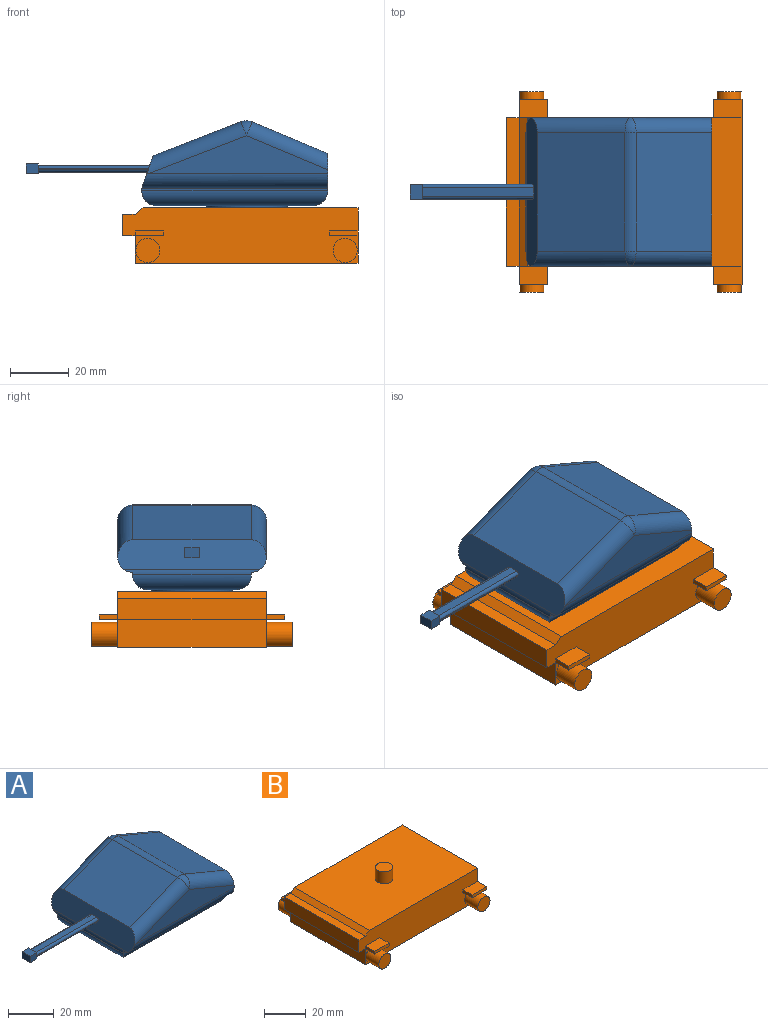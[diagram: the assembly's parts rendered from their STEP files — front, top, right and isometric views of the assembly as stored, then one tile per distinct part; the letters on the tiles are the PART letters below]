
ASSEMBLY  parts=2 mates=1
PART A: 41 faces, bbox 105.1x50.8x29.8 mm
  f0: cylinder r=11.12mm len=22.25mm, axis (0,0,1), area 471.8mm2, adj f2,f3
  f1: cylinder r=13.89mm len=27.79mm, axis (0,0,1), area 65.5mm2, adj f2,f7
  f2: plane 27.79x27.79mm, normal (0,0,-1), area 217.6mm2, adj f0,f1
  f3: plane 22.25x22.25mm, normal (0,0,-1), area 388.8mm2, adj f0
  f4: plane 40.64x0.05mm, normal (-1,0,0), area 2.2mm2, adj f5,f6,f36,f40
  f5: plane 63.5x0.92mm, normal (0,1,0), area 58.4mm2, adj f4,f33,f34,f38,f40
  f6: plane 63.5x0.92mm, normal (0,-1,0), area 58.4mm2, adj f4,f32,f33,f37,f40
  f7: plane 53.34x30.48mm, normal (0,0,-1), area 1019.4mm2, adj f1,f36,f37,f38,f39
  f8: plane 5.08x1.62mm, normal (1,0,0), area 3.5mm2, adj f9,f19,f20,f21,f22,f23
  f9: plane 5.08x4.19mm, normal (0,0,-1), area 21.3mm2, adj f8,f10,f19,f23
  f10: plane 5.08x3.37mm, normal (-1,0,0), area 17.1mm2, adj f9,f11,f19,f23
  f11: plane 5.08x4.19mm, normal (0,0,1), area 21.3mm2, adj f10,f12,f19,f23
  f12: plane 5.08x1.62mm, normal (1,0,0), area 3.5mm2, adj f11,f16,f17,f18,f19,f23
  f13: cylinder r=5.08mm len=40.64mm, axis (0,1,0), area 158.4mm2, adj f14,f15,f24,f27
  f14: sphere r=5.08mm, area 19.8mm2, adj f13,f25,f28
  f15: sphere r=5.08mm, area 19.8mm2, adj f13,f26,f30
  f16: cylinder r=1.02mm len=38.1mm, axis (1,0,0), area 60.6mm2, adj f12,f17,f23,f35
  f17: plane 38.1x3.05mm, normal (0,0,1), area 116.1mm2, adj f12,f16,f18,f35
  f18: cylinder r=1.02mm len=38.1mm, axis (-1,0,0), area 60.6mm2, adj f12,f17,f19,f35
  f19: plane 41.93x3.37mm, normal (0,1,0), area 19.4mm2, adj f8,f9,f10,f11,f12,f18,f20,f35
  f20: cylinder r=1.02mm len=37.69mm, axis (1,0,0), area 59.8mm2, adj f8,f19,f21,f35
  f21: plane 37.34x3.05mm, normal (0,0,-1), area 113.8mm2, adj f8,f20,f22,f35
  f22: cylinder r=1.02mm len=37.69mm, axis (-1,0,0), area 59.8mm2, adj f8,f21,f23,f35
  f23: plane 41.93x3.37mm, normal (0,-1,0), area 19.4mm2, adj f8,f9,f10,f11,f12,f16,f22,f35
  f24: plane 40.64x30.03mm, normal (-0.36,0,0.93), area 1309.1mm2, adj f13,f25,f30,f35
  f25: cylinder r=5.08mm len=35.79mm, axis (-0.93,0,-0.36), area 269.6mm2, adj f14,f24,f29,f34,f35
  f26: cylinder r=5.08mm len=29.72mm, axis (0.92,0,-0.39), area 229.4mm2, adj f15,f27,f31,f33
  f27: plane 40.64x25.79mm, normal (0.39,0,0.92), area 1136.8mm2, adj f13,f26,f28,f33
  f28: cylinder r=5.08mm len=29.72mm, axis (-0.92,0,0.39), area 229.4mm2, adj f14,f27,f29,f33
  f29: plane 60.93x12.87mm, normal (0,1,0), area 409mm2, adj f25,f28,f33,f34
  f30: cylinder r=5.08mm len=35.79mm, axis (0.93,0,0.36), area 269.6mm2, adj f15,f24,f31,f32,f35
  f31: plane 60.93x12.87mm, normal (0,-1,0), area 409mm2, adj f26,f30,f32,f33
  f32: cylinder r=5.08mm len=63.43mm, axis (-1,0,0), area 501.4mm2, adj f6,f30,f31,f33,f35,f40
  f33: plane 50.8x12.73mm, normal (1,0,0), area 614.2mm2, adj f5,f6,f26,f27,f28,f29,f31,f32
  f34: cylinder r=5.08mm len=63.43mm, axis (1,0,0), area 501.4mm2, adj f5,f25,f29,f33,f35,f40
  f35: plane 50.8x10.22mm, normal (-0.94,0,0.33), area 518.6mm2, adj f16,f17,f18,f19,f20,f21,f22,f23
  f36: cylinder r=5.08mm len=40.64mm, axis (0,1,0), area 294.8mm2, adj f4,f7,f37,f38
  f37: cylinder r=5.08mm len=63.5mm, axis (-1,0,0), area 477.2mm2, adj f6,f7,f36,f39
  f38: cylinder r=5.08mm len=63.5mm, axis (1,0,0), area 477.2mm2, adj f5,f7,f36,f39
  f39: cylinder r=5.08mm len=40.64mm, axis (0,1,0), area 294.8mm2, adj f7,f33,f37,f38
  f40: cylinder r=5.08mm len=46.16mm, axis (0,-1,0), area 72.8mm2, adj f4,f5,f6,f32,f34,f35
PART B: 38 faces, bbox 80.5x68.6x25.9 mm
  f0: plane 9.82x6.35mm, normal (0,0,-1), area 62.4mm2, adj f8,f11,f22,f25
  f1: plane 9.82x6.35mm, normal (0,0,-1), area 62.4mm2, adj f4,f11,f14,f18
  f2: plane 50.8x4.32mm, normal (0,0,-1), area 219.4mm2, adj f6,f10,f11,f27
  f3: plane 6.35x1.61mm, normal (-1,0,0), area 10.2mm2, adj f10,f12,f16,f17
  f4: plane 6.35x1.61mm, normal (-1,0,0), area 10.2mm2, adj f1,f11,f15,f18
  f5: plane 50.8x2.73mm, normal (-0.61,0,0.79), area 174.8mm2, adj f9,f10,f11,f26
  f6: plane 50.8x9.46mm, normal (-1,0,0), area 480.4mm2, adj f2,f7,f10,f11
  f7: plane 76.2x50.8mm, normal (0,0,-1), area 3871mm2, adj f6,f8,f10,f11
  f8: plane 63.5x18.91mm, normal (1,0,0), area 981.2mm2, adj f0,f7,f9,f10,f11,f20,f21,f23
  f9: plane 73.47x50.8mm, normal (0,0,1), area 3679mm2, adj f5,f8,f10,f11,f28
  f10: plane 80.52x18.91mm, normal (0,-1,0), area 1331.5mm2, adj f2,f3,f5,f6,f7,f8,f9,f12
  f11: plane 80.52x18.91mm, normal (0,1,0), area 1331.5mm2, adj f0,f1,f2,f4,f5,f6,f7,f8
  f12: plane 9.82x6.35mm, normal (0,0,1), area 62.4mm2, adj f3,f10,f13,f17
  f13: plane 6.35x1.61mm, normal (1,0,0), area 10.2mm2, adj f10,f12,f16,f17
  f14: plane 6.35x1.61mm, normal (1,0,0), area 10.2mm2, adj f1,f11,f15,f18
  f15: plane 9.82x6.35mm, normal (0,0,1), area 62.4mm2, adj f4,f11,f14,f18
  f16: plane 9.82x6.35mm, normal (0,0,-1), area 62.4mm2, adj f3,f10,f13,f17
  f17: plane 9.82x1.61mm, normal (0,-1,0), area 15.8mm2, adj f3,f12,f13,f16
  f18: plane 9.82x1.61mm, normal (0,1,0), area 15.8mm2, adj f1,f4,f14,f15
  f19: plane 6.35x1.61mm, normal (-1,0,0), area 10.2mm2, adj f10,f20,f23,f24
  f20: plane 9.82x6.35mm, normal (0,0,1), area 62.4mm2, adj f8,f10,f19,f24
  f21: plane 9.82x6.35mm, normal (0,0,1), area 62.4mm2, adj f8,f11,f22,f25
  f22: plane 6.35x1.61mm, normal (-1,0,0), area 10.2mm2, adj f0,f11,f21,f25
  f23: plane 9.82x6.35mm, normal (0,0,-1), area 62.4mm2, adj f8,f10,f19,f24
  f24: plane 9.82x1.61mm, normal (0,-1,0), area 15.8mm2, adj f8,f19,f20,f23
  f25: plane 9.82x1.61mm, normal (0,1,0), area 15.8mm2, adj f0,f8,f21,f22
  f26: plane 50.8x4.32mm, normal (0,0,1), area 219.4mm2, adj f5,f10,f11,f27
  f27: plane 50.8x7.36mm, normal (-1,0,0), area 373.7mm2, adj f2,f10,f11,f26
  f28: cylinder r=4.12mm len=8.25mm, axis (0,0,-1), area 181.4mm2, adj f9,f29
  f29: plane 8.25x8.25mm, normal (0,0,1), area 53.5mm2, adj f28
  f30: plane 8.25x8.25mm, normal (0,-1,0), area 53.5mm2, adj f31
  f31: cylinder r=4.12mm len=8.89mm, axis (0,1,0), area 230.4mm2, adj f10,f30
  f32: plane 8.25x8.25mm, normal (0,-1,0), area 53.5mm2, adj f33
  f33: cylinder r=4.12mm len=8.89mm, axis (0,1,0), area 230.4mm2, adj f10,f32
  f34: plane 8.25x8.25mm, normal (0,1,0), area 53.5mm2, adj f35
  f35: cylinder r=4.12mm len=8.89mm, axis (0,-1,0), area 230.4mm2, adj f11,f34
  f36: plane 8.25x8.25mm, normal (0,1,0), area 53.5mm2, adj f37
  f37: cylinder r=4.12mm len=8.89mm, axis (0,-1,0), area 230.4mm2, adj f11,f36
PLACE A t=(-94.92,-43,8.83)mm
PLACE B t=(-94.92,-43,-7.38)mm
MATE revolute A.f0 <-> B.f28  axis (0,0,-1) through (-94.92,-43,2.08)mm
